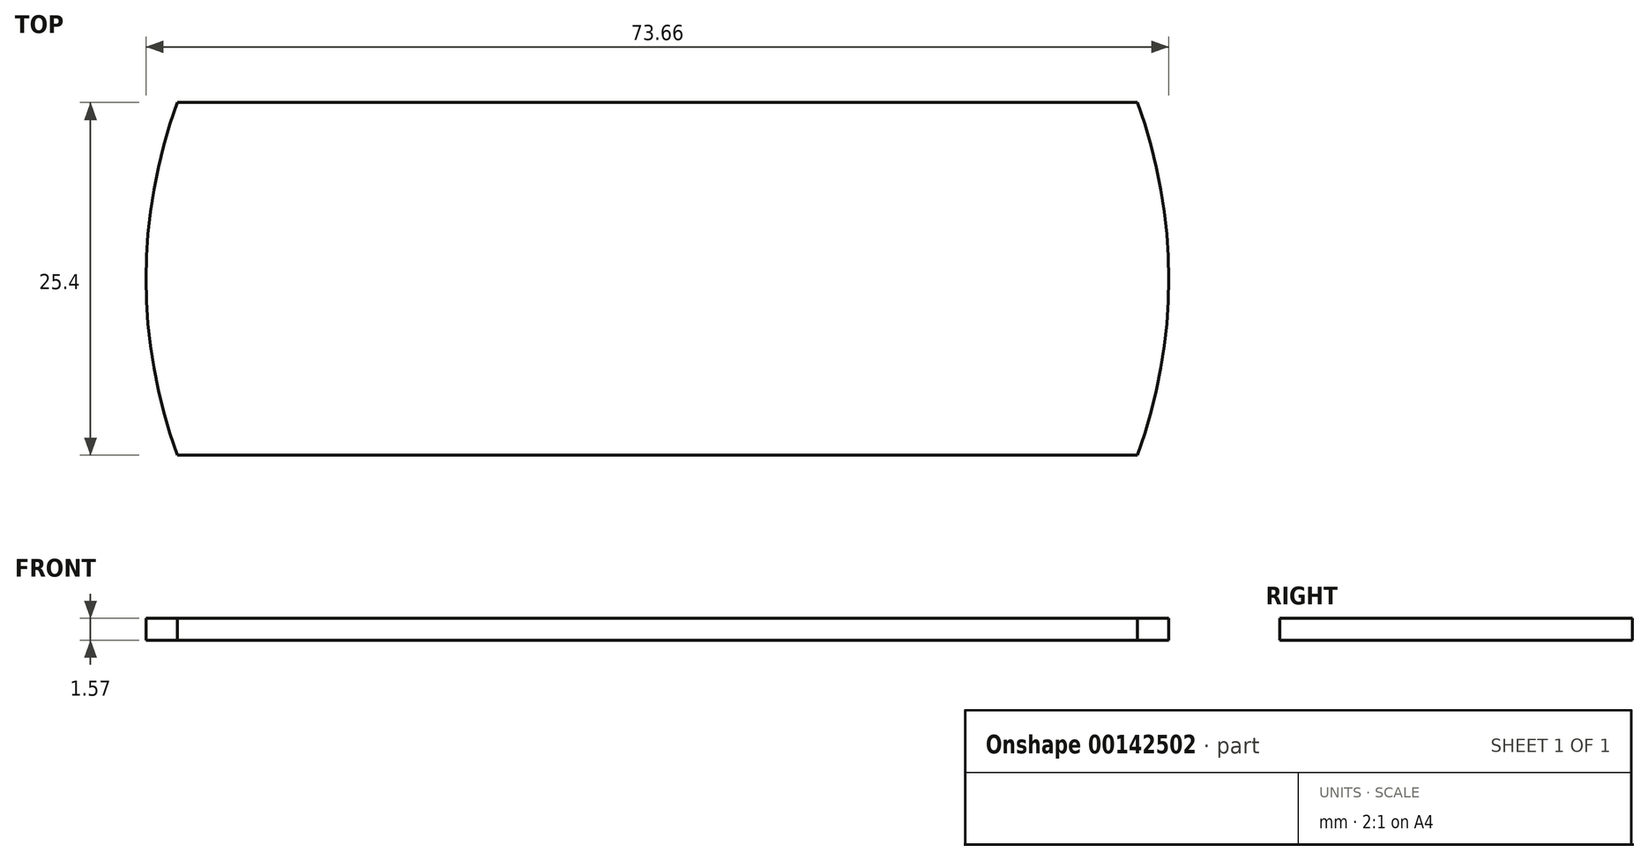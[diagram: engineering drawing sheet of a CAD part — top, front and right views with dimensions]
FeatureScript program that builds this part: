
annotation { "Feature Type Name" : "Feature", "Feature Type Description" : "" }
export const myFeature = defineFeature(function(context is Context, id is Id, definition is map)
    precondition{}
    {
        {
            var Q0;
            Q0=qCreatedBy(makeId("Top.planeOp"),FACE);
            var sketch = newSketch(context, id + "F0", { "sketchPlane" : qUnion([Q0])});
            skArc(sketch, "E0", {"start": v(-34.57, 12.7) * mm, "mid": v(-36.83, 0) * mm, "end": v(-34.57, -12.7) * mm});
            skLineSegment(sketch, "E1.bottom", {"start": v(-34.57, 12.7) * mm, "end": v(34.57, 12.7) * mm});
            skLineSegment(sketch, "E1.top", {"start": v(-34.57, -12.7) * mm, "end": v(34.57, -12.7) * mm});
            skArc(sketch, "E2.trimOffspring", {"start": v(34.57, -12.7) * mm, "mid": v(36.83, 0) * mm, "end": v(34.57, 12.7) * mm});
            skSolve(sketch);
        }
        {
            var Q0;
            Q0 = qSketchRegion(id + "F0", true);
            extrude(context, id + "F1", {"entities" : qUnion([Q0]), "depth" : 1.57 * mm});
        }
    });
